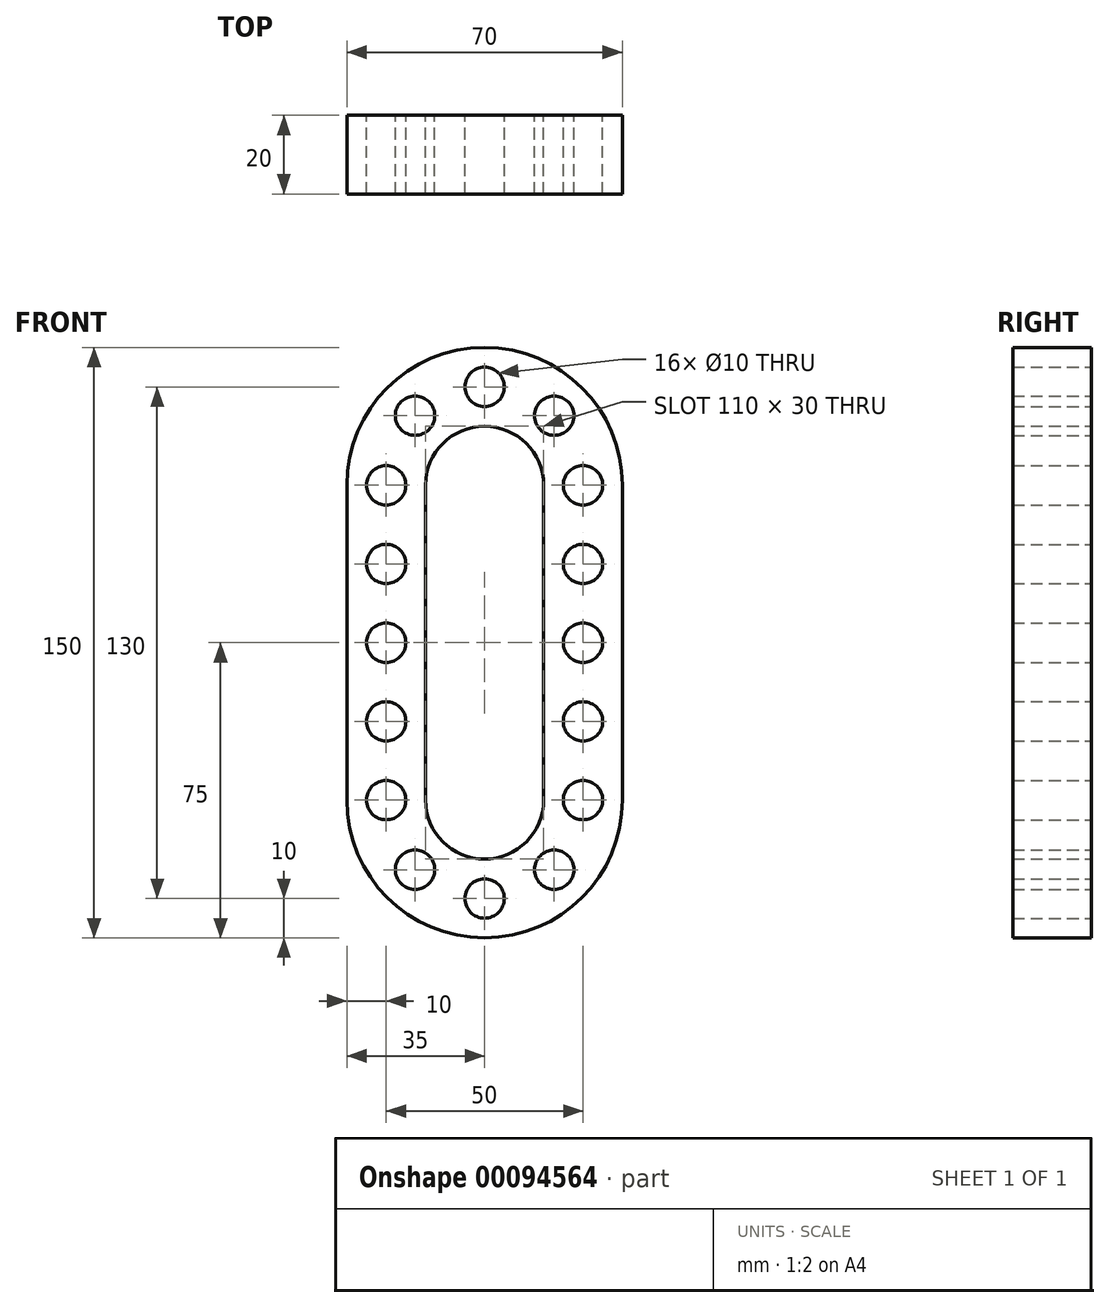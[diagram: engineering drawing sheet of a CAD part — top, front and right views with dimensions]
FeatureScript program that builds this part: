
annotation { "Feature Type Name" : "Feature", "Feature Type Description" : "" }
export const myFeature = defineFeature(function(context is Context, id is Id, definition is map)
    precondition{}
    {
        {
            var Q0;
            Q0=qCreatedBy(makeId("Front.planeOp"),FACE);
            var sketch = newSketch(context, id + "F0", { "sketchPlane" : qUnion([Q0])});
            skPoint(sketch, "E0", {"position": v(-25, 40) * mm});
            skLineSegment(sketch, "E1", {"start": v(-25, 40) * mm, "end": v(-25, 0) * mm, "construction": true});
            skArc(sketch, "E2", {"start": v(0, 65) * mm, "mid": v(-17.68, 57.68) * mm, "end": v(-25, 40) * mm, "construction": true});
            skArc(sketch, "E3.0.startCap", {"start": v(0, 75) * mm, "mid": v(10, 65) * mm, "end": v(0, 55) * mm, "construction": true});
            skArc(sketch, "E3.0.endCap", {"start": v(-15, 40) * mm, "mid": v(-25, 30) * mm, "end": v(-35, 40) * mm, "construction": true});
            skArc(sketch, "E3.0.left", {"start": v(0, 55) * mm, "mid": v(-10.6, 50.6) * mm, "end": v(-15, 40) * mm});
            skArc(sketch, "E3.0.right", {"start": v(0, 75) * mm, "mid": v(-24.75, 64.75) * mm, "end": v(-35, 40) * mm});
            skArc(sketch, "E3.1.startCap", {"start": v(-35, 40) * mm, "mid": v(-25, 50) * mm, "end": v(-15, 40) * mm, "construction": true});
            skArc(sketch, "E3.1.endCap", {"start": v(-15, 0) * mm, "mid": v(-25, -10) * mm, "end": v(-35, 0) * mm, "construction": true});
            skLineSegment(sketch, "E3.1.left", {"start": v(-15, 40) * mm, "end": v(-15, 0) * mm});
            skLineSegment(sketch, "E3.1.right", {"start": v(-35, 40) * mm, "end": v(-35, 0) * mm});
            skCircle(sketch, "E4", {"center": v(-25, 40) * mm, "radius": 5 * mm});
            skCircle(sketch, "E5.0.1.0", {"center": v(-25, 20) * mm, "radius": 5 * mm});
            skCircle(sketch, "E5.0.2.0", {"center": v(-25, 0) * mm, "radius": 5 * mm});
            skLineSegment(sketch, "E5.direction1", {"start": v(-25, 40) * mm, "end": v(0, 40) * mm, "construction": true});
            skLineSegment(sketch, "E5.direction2", {"start": v(-25, 40) * mm, "end": v(-25, 20) * mm, "construction": true});
            skPoint(sketch, "E6.1.0", {"position": v(-17.68, 57.68) * mm});
            skCircle(sketch, "E6.1.1", {"center": v(-17.68, 57.68) * mm, "radius": 5 * mm});
            skCircle(sketch, "E6.2.1", {"center": v(0, 65) * mm, "radius": 5 * mm});
            skLineSegment(sketch, "E6.anchor1", {"start": v(0, 40) * mm, "end": v(-25, 40) * mm, "construction": true});
            skLineSegment(sketch, "E6.anchor2", {"start": v(0, 40) * mm, "end": v(0, 65) * mm, "construction": true});
            skLineSegment(sketch, "E7", {"start": v(-35, 0) * mm, "end": v(-25, 0) * mm});
            skLineSegment(sketch, "E8", {"start": v(-25, 0) * mm, "end": v(-15, 0) * mm});
            skLineSegment(sketch, "E9", {"start": v(0, 75) * mm, "end": v(0, 65) * mm});
            skLineSegment(sketch, "E10", {"start": v(0.08, 64.36) * mm, "end": v(0, 55) * mm});
            skSolve(sketch);
        }
        {
            var Q0;
            {var subQ6=sQuery(id+"F0.wireOp",EDGE,"E3.0.left");Q0=makeQuery(id+"F0.imprint","IMPRINT",FACE,{"disambiguationData":[TD([[makeQuery(id+"F0.imprint","IMPRINT",EDGE,{"derivedFrom":subQ6}),-1.0]])]});}
            extrude(context, id + "F1", {"entities" : qUnion([Q0]), "depth" : 20 * mm});
        }
        {
            var Q0;
            Q0=makeQuery(id+"F1.opExtrude","SWEPT_BODY",BODY,{"disambiguationData":[OSD([sQuery(id+"F0.wireOp",EDGE,"E3.0.left"),sQuery(id+"F0.wireOp",EDGE,"E3.0.right"),sQuery(id+"F0.wireOp",EDGE,"E3.1.left"),sQuery(id+"F0.wireOp",EDGE,"E3.1.right"),sQuery(id+"F0.wireOp",EDGE,"E4"),sQuery(id+"F0.wireOp",EDGE,"E5.0.1.0"),sQuery(id+"F0.wireOp",EDGE,"E5.0.2.0"),sQuery(id+"F0.wireOp",EDGE,"E6.1.1"),sQuery(id+"F0.wireOp",EDGE,"E6.2.1"),sQuery(id+"F0.wireOp",EDGE,"E7"),sQuery(id+"F0.wireOp",EDGE,"E8"),sQuery(id+"F0.wireOp",EDGE,"E9"),sQuery(id+"F0.wireOp",EDGE,"E10")])]});
            var Q1;
            Q1=qCreatedBy(makeId("Right.planeOp"),FACE);
            mirror(context, id + "F2", {"operationType" : NewBodyOperationType.ADD, "entities" : qUnion([Q0]), "mirrorPlane" : qUnion([Q1])});
        }
        {
            var Q0;
            Q0=makeQuery(id+"F1.opExtrude","SWEPT_BODY",BODY,{"disambiguationData":[OSD([sQuery(id+"F0.wireOp",EDGE,"E3.0.left"),sQuery(id+"F0.wireOp",EDGE,"E3.0.right"),sQuery(id+"F0.wireOp",EDGE,"E3.1.left"),sQuery(id+"F0.wireOp",EDGE,"E3.1.right"),sQuery(id+"F0.wireOp",EDGE,"E4"),sQuery(id+"F0.wireOp",EDGE,"E5.0.1.0"),sQuery(id+"F0.wireOp",EDGE,"E5.0.2.0"),sQuery(id+"F0.wireOp",EDGE,"E6.1.1"),sQuery(id+"F0.wireOp",EDGE,"E6.2.1"),sQuery(id+"F0.wireOp",EDGE,"E7"),sQuery(id+"F0.wireOp",EDGE,"E8"),sQuery(id+"F0.wireOp",EDGE,"E9"),sQuery(id+"F0.wireOp",EDGE,"E10")])]});
            var Q1;
            Q1=qCreatedBy(makeId("Top.planeOp"),FACE);
            mirror(context, id + "F3", {"operationType" : NewBodyOperationType.ADD, "entities" : qUnion([Q0]), "mirrorPlane" : qUnion([Q1])});
        }
    });
